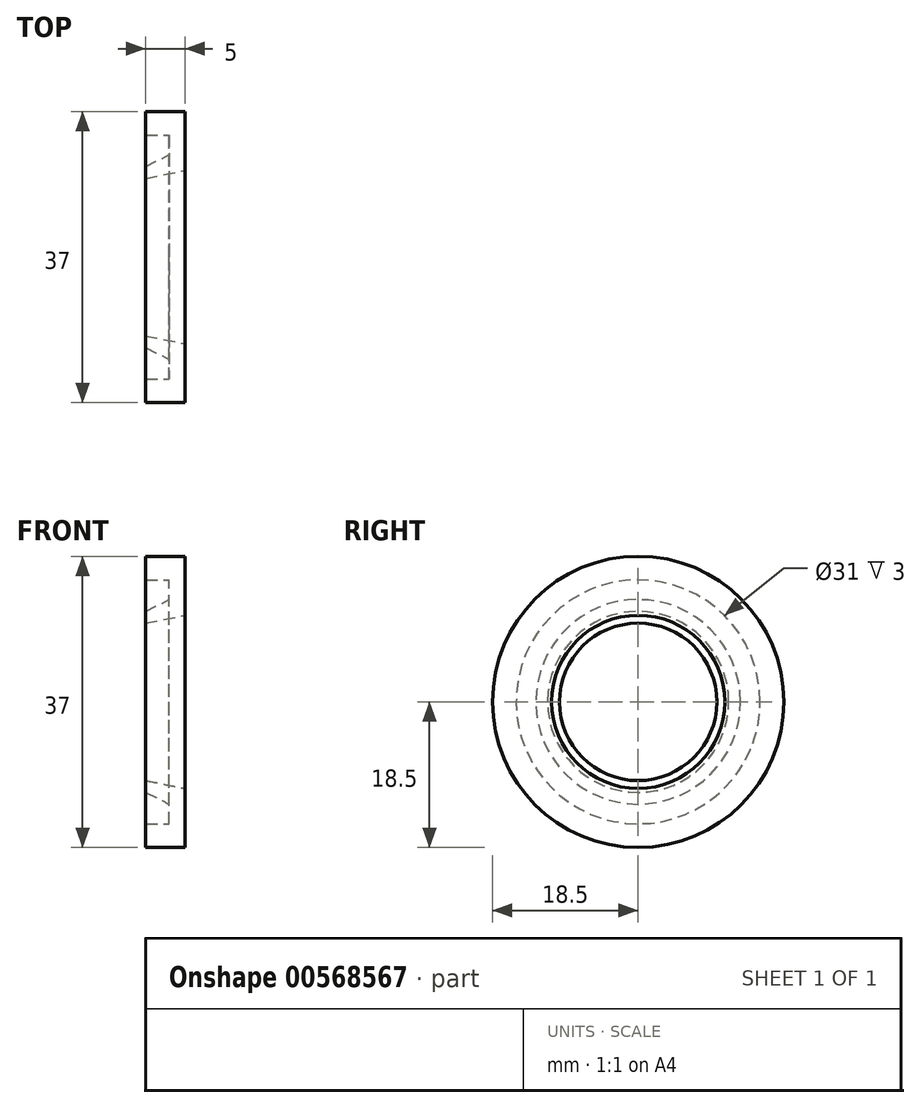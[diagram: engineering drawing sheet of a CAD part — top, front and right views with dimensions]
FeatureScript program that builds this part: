
annotation { "Feature Type Name" : "Feature", "Feature Type Description" : "" }
export const myFeature = defineFeature(function(context is Context, id is Id, definition is map)
    precondition{}
    {
        {
            var Q0;
            Q0=qCreatedBy(makeId("Front.planeOp"),FACE);
            var sketch = newSketch(context, id + "F0", { "sketchPlane" : qUnion([Q0])});
            skLineSegment(sketch, "E0", {"start": v(0, 0) * mm, "end": v(-45.82, 0) * mm, "construction": true});
            skLineSegment(sketch, "E1", {"start": v(0, 11) * mm, "end": v(-5, 10) * mm});
            skLineSegment(sketch, "E2", {"start": v(-5, 11.5) * mm, "end": v(-2, 13) * mm});
            skLineSegment(sketch, "E3", {"start": v(-2, 13) * mm, "end": v(-2, 15.5) * mm});
            skLineSegment(sketch, "E4", {"start": v(-2, 15.5) * mm, "end": v(-5, 15.5) * mm});
            skLineSegment(sketch, "E5", {"start": v(-5, 15.5) * mm, "end": v(-5, 18.5) * mm});
            skLineSegment(sketch, "E6", {"start": v(-5, 18.5) * mm, "end": v(0, 18.5) * mm});
            skLineSegment(sketch, "E7", {"start": v(0, 18.5) * mm, "end": v(0, 11) * mm});
            skLineSegment(sketch, "E8", {"start": v(-5, 10) * mm, "end": v(-5, 11.5) * mm});
            skSolve(sketch);
        }
        {
            var Q0;
            Q0=makeQuery(id+"F0.imprint","IMPRINT",FACE,{"disambiguationData":[TD([[makeQuery(id+"F0.imprint","IMPRINT",EDGE,{"derivedFrom":sQuery(id+"F0.wireOp",EDGE,"E1")}),-1.0]])]});
            var Q1;
            Q1=sQuery(id+"F0.wireOp",EDGE,"E0");
            revolve(context, id + "F1", {"entities" : qUnion([Q0]), "axis" : qUnion([Q1]), "revolveType" : RevolveType.FULL});
        }
    });
